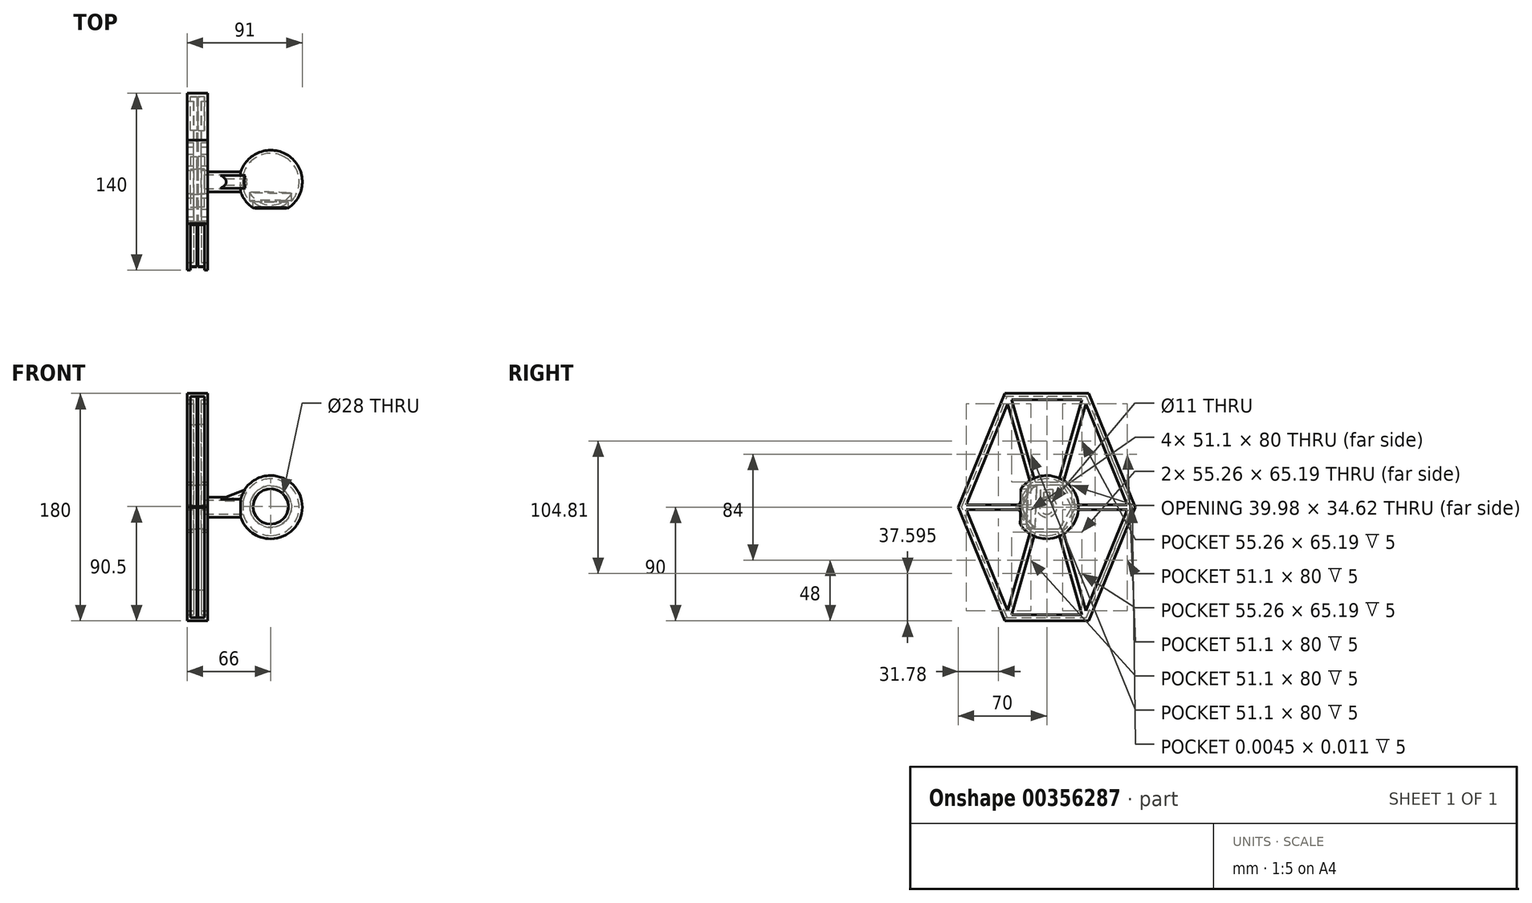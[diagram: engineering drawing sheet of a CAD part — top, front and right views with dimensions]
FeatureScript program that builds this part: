
annotation { "Feature Type Name" : "Feature", "Feature Type Description" : "" }
export const myFeature = defineFeature(function(context is Context, id is Id, definition is map)
    precondition{}
    {
        {
            var Q0;
            Q0=qCreatedBy(makeId("Front.planeOp"),FACE);
            var sketch = newSketch(context, id + "F0", { "sketchPlane" : qUnion([Q0])});
            skArc(sketch, "E0", {"start": v(0, -25) * mm, "mid": v(25, 0) * mm, "end": v(0, 25) * mm});
            skLineSegment(sketch, "E1", {"start": v(0, 25) * mm, "end": v(0, -25) * mm});
            skSolve(sketch);
        }
        {
            var Q0;
            Q0=qSketchRegion(id+"F0",true);
            var Q1;
            Q1=sQuery(id+"F0.wireOp",EDGE,"E1");
            revolve(context, id + "F1", {"entities" : qUnion([Q0]), "axis" : qUnion([Q1]), "revolveType" : RevolveType.FULL});
        }
        {
            var Q0;
            Q0=qCreatedBy(makeId("Front.planeOp"),FACE);
            var sketch = newSketch(context, id + "F2", { "sketchPlane" : qUnion([Q0])});
            skLineSegment(sketch, "E2.bottom", {"start": v(0, 0) * mm, "end": v(-55, 0) * mm});
            skLineSegment(sketch, "E2.top", {"start": v(0, 8) * mm, "end": v(-55, 8) * mm});
            skLineSegment(sketch, "E2.left", {"start": v(0, 0) * mm, "end": v(0, 8) * mm});
            skLineSegment(sketch, "E2.right", {"start": v(-55, 0) * mm, "end": v(-55, 8) * mm});
            skSolve(sketch);
        }
        {
            var Q0;
            Q0=qSketchRegion(id+"F2",true);
            var Q1;
            Q1=sQuery(id+"F2.wireOp",EDGE,"E2.bottom");
            revolve(context, id + "F3", {"operationType" : NewBodyOperationType.ADD, "entities" : qUnion([Q0]), "axis" : qUnion([Q1]), "revolveType" : RevolveType.FULL});
        }
        {
            var Q0;
            Q0=makeQuery(id+"F3.opRevolve","SWEPT_FACE",FACE,{"disambiguationData":[OSD([sQuery(id+"F2.wireOp",EDGE,"E2.right")])]});
            var sketch = newSketch(context, id + "F4", { "sketchPlane" : qUnion([Q0])});
            skLineSegment(sketch, "E3", {"start": v(0, 90) * mm, "end": v(-33.06, 90) * mm});
            skLineSegment(sketch, "E4", {"start": v(-33.06, 90) * mm, "end": v(-70, 0) * mm});
            skLineSegment(sketch, "E5", {"start": v(-70, 0) * mm, "end": v(0, 0) * mm, "construction": true});
            skLineSegment(sketch, "E6", {"start": v(0, 0) * mm, "end": v(0, 90) * mm, "construction": true});
            skLineSegment(sketch, "E7.MirrorCS", {"start": v(-33.06, -90) * mm, "end": v(-70, 0) * mm});
            skLineSegment(sketch, "E8.MirrorCS", {"start": v(0, -90) * mm, "end": v(-33.06, -90) * mm});
            skLineSegment(sketch, "E9.MirrorCS", {"start": v(0, 90) * mm, "end": v(33.06, 90) * mm});
            skLineSegment(sketch, "E10.MirrorCS", {"start": v(33.06, 90) * mm, "end": v(70, 0) * mm});
            skLineSegment(sketch, "E11.MirrorCS", {"start": v(33.06, -90) * mm, "end": v(70, 0) * mm});
            skLineSegment(sketch, "E12.MirrorCS", {"start": v(0, -90) * mm, "end": v(33.06, -90) * mm});
            skSolve(sketch);
        }
        {
            var Q0;
            Q0=qSketchRegion(id+"F4",true);
            extrude(context, id + "F5", {"entities" : qUnion([Q0]), "operationType" : NewBodyOperationType.ADD, "depth" : 6 * mm});
        }
        {
            var Q0;
            Q0=makeQuery(id+"F5.opExtrude","CAP_FACE",FACE,{"disambiguationData":[OSD([sQuery(id+"F4.wireOp",EDGE,"E3"),sQuery(id+"F4.wireOp",EDGE,"E4"),sQuery(id+"F4.wireOp",EDGE,"E7.MirrorCS"),sQuery(id+"F4.wireOp",EDGE,"E8.MirrorCS"),sQuery(id+"F4.wireOp",EDGE,"E9.MirrorCS"),sQuery(id+"F4.wireOp",EDGE,"E10.MirrorCS"),sQuery(id+"F4.wireOp",EDGE,"E11.MirrorCS"),sQuery(id+"F4.wireOp",EDGE,"E12.MirrorCS")])],"isStart":false});
            var sketch = newSketch(context, id + "F6", { "sketchPlane" : qUnion([Q0])});
            skLineSegment(sketch, "E13.0", {"start": v(-30.94, 82) * mm, "end": v(-12.67, 17.68) * mm});
            skLineSegment(sketch, "E14.0", {"start": v(-27.63, 85) * mm, "end": v(-9.12, 19.81) * mm});
            skLineSegment(sketch, "E15.0", {"start": v(-63.77, -2) * mm, "end": v(-21.72, -2) * mm});
            skLineSegment(sketch, "E16.0", {"start": v(-63.77, 2) * mm, "end": v(-21.72, 2) * mm});
            skLineSegment(sketch, "E17", {"start": v(0, 0) * mm, "end": v(0, -57.76) * mm, "construction": true});
            skLineSegment(sketch, "E18", {"start": v(0, 0) * mm, "end": v(92.77, 0) * mm, "construction": true});
            skLineSegment(sketch, "E19.MirrorCS", {"start": v(63.77, -2) * mm, "end": v(21.72, -2) * mm});
            skLineSegment(sketch, "E20.MirrorCS", {"start": v(63.77, 2) * mm, "end": v(21.72, 2) * mm});
            skLineSegment(sketch, "E21.MirrorCS", {"start": v(30.94, 82) * mm, "end": v(12.67, 17.68) * mm});
            skLineSegment(sketch, "E22.MirrorCS", {"start": v(27.63, 85) * mm, "end": v(9.12, 19.81) * mm});
            skLineSegment(sketch, "E23.MirrorCS", {"start": v(-30.94, -82) * mm, "end": v(-12.67, -17.68) * mm});
            skLineSegment(sketch, "E24.MirrorCS", {"start": v(-27.63, -85) * mm, "end": v(-9.12, -19.81) * mm});
            skLineSegment(sketch, "E25.MirrorCS", {"start": v(27.63, -85) * mm, "end": v(9.12, -19.81) * mm});
            skLineSegment(sketch, "E26.MirrorCS", {"start": v(30.94, -82) * mm, "end": v(12.67, -17.68) * mm});
            skLineSegment(sketch, "E27.0", {"start": v(-9.12, 19.81) * mm, "end": v(9.12, 19.81) * mm});
            skLineSegment(sketch, "E27.1", {"start": v(12.67, 17.68) * mm, "end": v(21.72, 2) * mm});
            skLineSegment(sketch, "E27.2", {"start": v(21.72, -2) * mm, "end": v(12.67, -17.68) * mm});
            skLineSegment(sketch, "E27.3", {"start": v(9.12, -19.81) * mm, "end": v(-9.12, -19.81) * mm});
            skLineSegment(sketch, "E27.4", {"start": v(-12.67, -17.68) * mm, "end": v(-21.72, -2) * mm});
            skLineSegment(sketch, "E27.5", {"start": v(-21.72, 2) * mm, "end": v(-12.67, 17.68) * mm});
            skPoint(sketch, "E27.0.midPoint", {"position": v(0, 19.81) * mm});
            skPoint(sketch, "E28.end.orphan", {"position": v(-10.36, 9.54) * mm});
            skPoint(sketch, "E28.start.orphan", {"position": v(-6.97, 12.24) * mm});
            skPoint(sketch, "E29.orphan", {"position": v(-11.44, 19.81) * mm});
            skPoint(sketch, "E30.end.orphan", {"position": v(6.97, 12.24) * mm});
            skPoint(sketch, "E30.start.orphan", {"position": v(10.36, 9.54) * mm});
            skPoint(sketch, "E31.orphan", {"position": v(11.44, 19.81) * mm});
            skPoint(sketch, "E32.orphan", {"position": v(14.09, 2) * mm});
            skPoint(sketch, "E33.MirrorCS.end.orphan", {"position": v(14.09, -2) * mm});
            skPoint(sketch, "E34.end.orphan", {"position": v(10.36, -9.54) * mm});
            skPoint(sketch, "E35.orphan", {"position": v(6.97, -12.24) * mm});
            skPoint(sketch, "E36.end.orphan", {"position": v(-6.97, -12.24) * mm});
            skPoint(sketch, "E36.start.orphan", {"position": v(-10.36, -9.54) * mm});
            skPoint(sketch, "E37.end.orphan", {"position": v(-14.09, -2) * mm});
            skPoint(sketch, "E37.start.orphan", {"position": v(-14.09, 2) * mm});
            skLineSegment(sketch, "E38.0", {"start": v(-33.06, 90) * mm, "end": v(-70, 0) * mm});
            skLineSegment(sketch, "E38.1", {"start": v(-33.06, -90) * mm, "end": v(33.06, -90) * mm});
            skLineSegment(sketch, "E38.2", {"start": v(33.06, -90) * mm, "end": v(70, 0) * mm});
            skLineSegment(sketch, "E38.3", {"start": v(-70, 0) * mm, "end": v(-33.06, -90) * mm});
            skLineSegment(sketch, "E38.4", {"start": v(70, 0) * mm, "end": v(33.06, 90) * mm});
            skLineSegment(sketch, "E38.5", {"start": v(33.06, 90) * mm, "end": v(-33.06, 90) * mm});
            skLineSegment(sketch, "E39.0", {"start": v(27.63, 85) * mm, "end": v(-27.63, 85) * mm});
            skLineSegment(sketch, "E39.1", {"start": v(-63.77, -2) * mm, "end": v(-30.94, -82) * mm});
            skLineSegment(sketch, "E39.2", {"start": v(-27.63, -85) * mm, "end": v(27.63, -85) * mm});
            skLineSegment(sketch, "E39.3", {"start": v(-30.94, 82) * mm, "end": v(-63.77, 2) * mm});
            skLineSegment(sketch, "E39.4", {"start": v(30.94, -82) * mm, "end": v(63.77, -2) * mm});
            skLineSegment(sketch, "E39.5", {"start": v(63.77, 2) * mm, "end": v(30.94, 82) * mm});
            skPoint(sketch, "E40.orphan", {"position": v(-31.64, 84.45) * mm});
            skPoint(sketch, "E41.orphan", {"position": v(-27.79, 85.55) * mm});
            skPoint(sketch, "E42.orphan", {"position": v(31.64, 84.45) * mm});
            skPoint(sketch, "E43.orphan", {"position": v(27.79, 85.55) * mm});
            skPoint(sketch, "E44.orphan", {"position": v(64.6, 2) * mm});
            skPoint(sketch, "E45.MirrorCS.end.orphan", {"position": v(64.6, -2) * mm});
            skPoint(sketch, "E46.orphan", {"position": v(31.64, -84.45) * mm});
            skPoint(sketch, "E47.orphan", {"position": v(27.79, -85.55) * mm});
            skPoint(sketch, "E48.orphan", {"position": v(-31.64, -84.45) * mm});
            skPoint(sketch, "E49.orphan", {"position": v(-27.79, -85.55) * mm});
            skPoint(sketch, "E50.orphan", {"position": v(-64.6, 2) * mm});
            skPoint(sketch, "E51.orphan", {"position": v(-64.6, -2) * mm});
            skSolve(sketch);
        }
        {
            var Q0;
            Q0=qSketchRegion(id+"F6",true);
            extrude(context, id + "F7", {"entities" : qUnion([Q0]), "operationType" : NewBodyOperationType.ADD, "depth" : 5 * mm, "hasSecondDirection" : true, "secondDirectionOppositeDirection" : true, "secondDirectionDepth" : 11 * mm});
        }
        {
            var Q0;
            Q0=qCreatedBy(makeId("Front.planeOp"),FACE);
            var sketch = newSketch(context, id + "F8", { "sketchPlane" : qUnion([Q0])});
            skLineSegment(sketch, "E52", {"start": v(-42.11, 5.22) * mm, "end": v(-8.42, 18.7) * mm});
            skLineSegment(sketch, "E53", {"start": v(-8.42, 18.7) * mm, "end": v(-8.42, 4.21) * mm});
            skLineSegment(sketch, "E54", {"start": v(-8.42, 4.21) * mm, "end": v(-42.11, 5.22) * mm});
            skSolve(sketch);
        }
        {
            var Q0;
            Q0=makeQuery(id+"F8.imprint","IMPRINT",FACE,{"disambiguationData":[TD([[makeQuery(id+"F8.imprint","IMPRINT",EDGE,{"derivedFrom":sQuery(id+"F8.wireOp",EDGE,"E52")}),-1.0]])]});
            extrude(context, id + "F9", {"entities" : qUnion([Q0]), "operationType" : NewBodyOperationType.ADD, "depth" : 5 * mm, "hasSecondDirection" : true, "secondDirectionOppositeDirection" : true, "secondDirectionDepth" : 5 * mm});
        }
        {
            var Q0;
            Q0=qCreatedBy(makeId("Front.planeOp"),FACE);
            var sketch = newSketch(context, id + "F10", { "sketchPlane" : qUnion([Q0])});
            skCircle(sketch, "E55", {"center": v(0, 0.5) * mm, "radius": 14 * mm});
            skSolve(sketch);
        }
        {
            var Q0;
            Q0=qSketchRegion(id+"F10",true);
            extrude(context, id + "F11", {"entities" : qUnion([Q0]), "operationType" : NewBodyOperationType.REMOVE, "depth" : 25 * mm});
        }
        {
            var Q0;
            Q0=qCreatedBy(makeId("Front.planeOp"),FACE);
            var sketch = newSketch(context, id + "F12", { "sketchPlane" : qUnion([Q0])});
            skArc(sketch, "E56", {"start": v(0.34, -20.83) * mm, "mid": v(21.34, 0.34) * mm, "end": v(0, 21.17) * mm});
            skLineSegment(sketch, "E57", {"start": v(0, 21.17) * mm, "end": v(0.34, -20.83) * mm});
            skSolve(sketch);
        }
        {
            var Q0;
            Q0=qSketchRegion(id+"F12",true);
            var Q1;
            Q1=sQuery(id+"F12.wireOp",EDGE,"E57");
            revolve(context, id + "F13", {"operationType" : NewBodyOperationType.ADD, "entities" : qUnion([Q0]), "axis" : qUnion([Q1]), "revolveType" : RevolveType.FULL});
        }
        {
            var Q0;
            Q0=makeQuery(id+"F7.boolean.opBoolean","MERGE",FACE,{"derivedFrom":[makeQuery(id+"F5.opExtrude","SWEPT_FACE",FACE,{"disambiguationData":[OSD([sQuery(id+"F4.wireOp",EDGE,"E10.MirrorCS")])]}),makeQuery(id+"F7.opExtrude","SWEPT_FACE",FACE,{"disambiguationData":[OSD([sQuery(id+"F6.wireOp",EDGE,"E38.4")])]})]});
            var Q1;
            Q1=makeQuery(id+"F7.boolean.opBoolean","MERGE",FACE,{"derivedFrom":[makeQuery(id+"F5.opExtrude","SWEPT_FACE",FACE,{"disambiguationData":[OSD([sQuery(id+"F4.wireOp",EDGE,"E11.MirrorCS")])]}),makeQuery(id+"F7.opExtrude","SWEPT_FACE",FACE,{"disambiguationData":[OSD([sQuery(id+"F6.wireOp",EDGE,"E38.2")])]})]});
            var Q2;
            Q2=makeQuery(id+"Ft8bpTyiOZFzOle_1.1.F7.boolean.opBoolean","MERGE",FACE,{"derivedFrom":[makeQuery(id+"Ft8bpTyiOZFzOle_1.1.F5.opExtrude","SWEPT_FACE",FACE,{"disambiguationData":[OSD([sQuery(id+"F4.wireOp",EDGE,"E11.MirrorCS")])]}),makeQuery(id+"Ft8bpTyiOZFzOle_1.1.F7.opExtrude","SWEPT_FACE",FACE,{"disambiguationData":[OSD([sQuery(id+"F6.wireOp",EDGE,"E38.2")])]})]});
            var Q3;
            Q3=makeQuery(id+"Ft8bpTyiOZFzOle_1.1.F7.boolean.opBoolean","MERGE",FACE,{"derivedFrom":[makeQuery(id+"Ft8bpTyiOZFzOle_1.1.F5.opExtrude","SWEPT_FACE",FACE,{"disambiguationData":[OSD([sQuery(id+"F4.wireOp",EDGE,"E10.MirrorCS")])]}),makeQuery(id+"Ft8bpTyiOZFzOle_1.1.F7.opExtrude","SWEPT_FACE",FACE,{"disambiguationData":[OSD([sQuery(id+"F6.wireOp",EDGE,"E38.4")])]})]});
            shell(context, id + "F14", {"entities" : qUnion([Q0, Q1, Q2, Q3]), "thickness" : 2.5 * mm});
        }
    });
